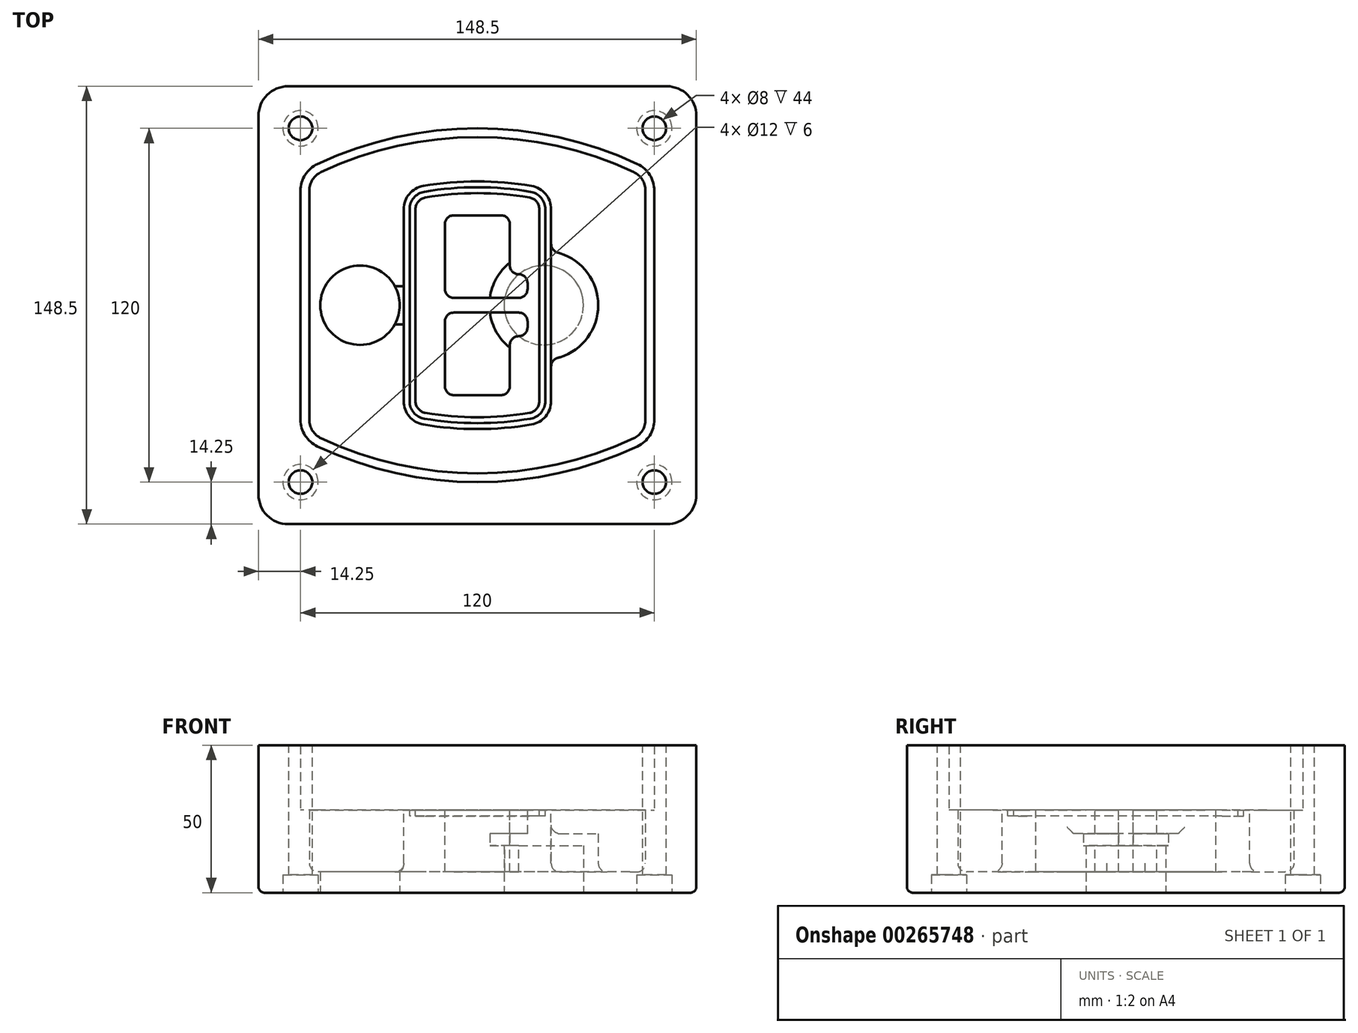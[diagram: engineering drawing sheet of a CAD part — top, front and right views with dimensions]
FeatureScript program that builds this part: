
annotation { "Feature Type Name" : "Feature", "Feature Type Description" : "" }
export const myFeature = defineFeature(function(context is Context, id is Id, definition is map)
    precondition{}
    {
        {
            var Q0;
            Q0=qCreatedBy(makeId("Top.planeOp"),FACE);
            var sketch = newSketch(context, id + "F0", { "sketchPlane" : qUnion([Q0])});
            skPoint(sketch, "E0.rect.middle", {"position": v(0, 0) * mm});
            skLineSegment(sketch, "E1.bottom", {"start": v(-64.25, -74.25) * mm, "end": v(64.25, -74.25) * mm});
            skLineSegment(sketch, "E1.top", {"start": v(-64.25, 74.25) * mm, "end": v(64.25, 74.25) * mm});
            skLineSegment(sketch, "E1.left", {"start": v(-74.25, -64.25) * mm, "end": v(-74.25, 64.25) * mm});
            skLineSegment(sketch, "E1.right", {"start": v(74.25, -64.25) * mm, "end": v(74.25, 64.25) * mm});
            skLineSegment(sketch, "E2", {"start": v(-74.25, 74.25) * mm, "end": v(74.25, -74.25) * mm, "construction": true});
            skLineSegment(sketch, "E3", {"start": v(74.25, 74.25) * mm, "end": v(-74.25, -74.25) * mm, "construction": true});
            skCircle(sketch, "E4", {"center": v(-60, 60) * mm, "radius": 4 * mm});
            skCircle(sketch, "E5", {"center": v(60, 60) * mm, "radius": 4 * mm});
            skCircle(sketch, "E6", {"center": v(60, -60) * mm, "radius": 4 * mm});
            skCircle(sketch, "E7", {"center": v(-60, -60) * mm, "radius": 4 * mm});
            skLineSegment(sketch, "E8", {"start": v(-60, 60) * mm, "end": v(60, 60) * mm, "construction": true});
            skLineSegment(sketch, "E9", {"start": v(60, 60) * mm, "end": v(60, -60) * mm, "construction": true});
            skLineSegment(sketch, "E10", {"start": v(60, -60) * mm, "end": v(-60, -60) * mm, "construction": true});
            skLineSegment(sketch, "E11", {"start": v(-60, -60) * mm, "end": v(-60, 60) * mm, "construction": true});
            skLineSegment(sketch, "E12", {"start": v(-60, 38.83) * mm, "end": v(-60, -38.83) * mm});
            skLineSegment(sketch, "E13", {"start": v(60, 38.83) * mm, "end": v(60, -38.83) * mm});
            skArc(sketch, "E14", {"start": v(54.26, 47.88) * mm, "mid": v(0, 60) * mm, "end": v(-54.26, 47.88) * mm});
            skArc(sketch, "E15", {"start": v(-54.26, -47.88) * mm, "mid": v(0, -60) * mm, "end": v(54.26, -47.88) * mm});
            skLineSegment(sketch, "E16", {"start": v(-60, 0) * mm, "end": v(60, 0) * mm, "construction": true});
            skPoint(sketch, "E17.visualSharp", {"position": v(-60, -45) * mm});
            skArc(sketch, "E17.filletArc", {"start": v(-60, -38.83) * mm, "mid": v(-58.44, -44.2) * mm, "end": v(-54.26, -47.88) * mm});
            skPoint(sketch, "E18.visualSharp", {"position": v(-60, 45) * mm});
            skArc(sketch, "E18.filletArc", {"start": v(-54.26, 47.88) * mm, "mid": v(-58.44, 44.2) * mm, "end": v(-60, 38.83) * mm});
            skPoint(sketch, "E19.visualSharp", {"position": v(60, 45) * mm});
            skArc(sketch, "E19.filletArc", {"start": v(60, 38.83) * mm, "mid": v(58.44, 44.2) * mm, "end": v(54.26, 47.88) * mm});
            skPoint(sketch, "E20.visualSharp", {"position": v(60, -45) * mm});
            skArc(sketch, "E20.filletArc", {"start": v(54.26, -47.88) * mm, "mid": v(58.44, -44.2) * mm, "end": v(60, -38.83) * mm});
            skPoint(sketch, "E21.visualSharp", {"position": v(-74.25, 74.25) * mm});
            skArc(sketch, "E21.filletArc", {"start": v(-64.25, 74.25) * mm, "mid": v(-71.32, 71.32) * mm, "end": v(-74.25, 64.25) * mm});
            skPoint(sketch, "E22.visualSharp", {"position": v(74.25, 74.25) * mm});
            skArc(sketch, "E22.filletArc", {"start": v(74.25, 64.25) * mm, "mid": v(71.32, 71.32) * mm, "end": v(64.25, 74.25) * mm});
            skPoint(sketch, "E23.visualSharp", {"position": v(74.25, -74.25) * mm});
            skArc(sketch, "E23.filletArc", {"start": v(64.25, -74.25) * mm, "mid": v(71.32, -71.32) * mm, "end": v(74.25, -64.25) * mm});
            skPoint(sketch, "E24.visualSharp", {"position": v(-74.25, -74.25) * mm});
            skArc(sketch, "E24.filletArc", {"start": v(-74.25, -64.25) * mm, "mid": v(-71.32, -71.32) * mm, "end": v(-64.25, -74.25) * mm});
            skArc(sketch, "E25.0", {"start": v(57, 38.83) * mm, "mid": v(55.9, 42.58) * mm, "end": v(52.98, 45.17) * mm});
            skLineSegment(sketch, "E25.1", {"start": v(57, 38.83) * mm, "end": v(57, -38.83) * mm});
            skArc(sketch, "E25.2", {"start": v(52.98, -45.17) * mm, "mid": v(55.9, -42.58) * mm, "end": v(57, -38.83) * mm});
            skArc(sketch, "E25.3", {"start": v(-52.98, -45.17) * mm, "mid": v(0, -57) * mm, "end": v(52.98, -45.17) * mm});
            skArc(sketch, "E25.4", {"start": v(-57, -38.83) * mm, "mid": v(-55.9, -42.58) * mm, "end": v(-52.98, -45.17) * mm});
            skArc(sketch, "E25.5", {"start": v(52.98, 45.17) * mm, "mid": v(0, 57) * mm, "end": v(-52.98, 45.17) * mm});
            skLineSegment(sketch, "E25.6", {"start": v(-57, 38.83) * mm, "end": v(-57, -38.83) * mm});
            skArc(sketch, "E25.7", {"start": v(-52.98, 45.17) * mm, "mid": v(-55.9, 42.58) * mm, "end": v(-57, 38.83) * mm});
            skArc(sketch, "E26.0", {"start": v(-55.96, 51.5) * mm, "mid": v(-61.82, 46.33) * mm, "end": v(-64, 38.83) * mm});
            skArc(sketch, "E26.1", {"start": v(55.96, 51.5) * mm, "mid": v(0, 64) * mm, "end": v(-55.96, 51.5) * mm});
            skArc(sketch, "E26.2", {"start": v(64, 38.83) * mm, "mid": v(61.82, 46.33) * mm, "end": v(55.96, 51.5) * mm});
            skLineSegment(sketch, "E26.3", {"start": v(64, 38.83) * mm, "end": v(64, -38.83) * mm});
            skArc(sketch, "E26.4", {"start": v(55.96, -51.5) * mm, "mid": v(61.82, -46.33) * mm, "end": v(64, -38.83) * mm});
            skLineSegment(sketch, "E26.5", {"start": v(-64, 38.83) * mm, "end": v(-64, -38.83) * mm});
            skArc(sketch, "E26.6", {"start": v(-55.96, -51.5) * mm, "mid": v(0, -64) * mm, "end": v(55.96, -51.5) * mm});
            skArc(sketch, "E26.7", {"start": v(-64, -38.83) * mm, "mid": v(-61.82, -46.33) * mm, "end": v(-55.96, -51.5) * mm});
            skSolve(sketch);
        }
        {
            var Q0;
            Q0=makeQuery(id+"F0.imprint","IMPRINT",FACE,{"disambiguationData":[TD([[makeQuery(id+"F0.imprint","IMPRINT",EDGE,{"derivedFrom":sQuery(id+"F0.wireOp",EDGE,"E1.bottom")}),1.0]])]});
            var Q1;
            Q1=makeQuery(id+"F0.imprint","IMPRINT",FACE,{"disambiguationData":[TD([[makeQuery(id+"F0.imprint","IMPRINT",EDGE,{"derivedFrom":sQuery(id+"F0.wireOp",EDGE,"E12")}),1.0]])]});
            var Q2;
            Q2=makeQuery(id+"F0.imprint","IMPRINT",FACE,{"disambiguationData":[TD([[makeQuery(id+"F0.imprint","IMPRINT",EDGE,{"derivedFrom":sQuery(id+"F0.wireOp",EDGE,"E25.0")}),1.0]])]});
            var Q3;
            Q3=makeQuery(id+"F0.imprint","IMPRINT",FACE,{"disambiguationData":[TD([[makeQuery(id+"F0.imprint","IMPRINT",EDGE,{"derivedFrom":sQuery(id+"F0.wireOp",EDGE,"E12")}),-1.0]])]});
            extrude(context, id + "F1", {"entities" : qUnion([Q0, Q1, Q2, Q3]), "oppositeDirection" : true, "depth" : 25 * mm});
        }
        {
            var Q0;
            Q0=makeQuery(id+"F0.imprint","IMPRINT",FACE,{"disambiguationData":[TD([[makeQuery(id+"F0.imprint","IMPRINT",EDGE,{"derivedFrom":sQuery(id+"F0.wireOp",EDGE,"E12")}),1.0]])]});
            extrude(context, id + "F2", {"entities" : qUnion([Q0]), "operationType" : NewBodyOperationType.ADD, "depth" : 3 * mm});
        }
        {
            var Q0;
            Q0=makeQuery(id+"F0.imprint","IMPRINT",FACE,{"disambiguationData":[TD([[makeQuery(id+"F0.imprint","IMPRINT",EDGE,{"derivedFrom":sQuery(id+"F0.wireOp",EDGE,"E25.0")}),1.0]])]});
            extrude(context, id + "F3", {"entities" : qUnion([Q0]), "operationType" : NewBodyOperationType.REMOVE, "oppositeDirection" : true, "depth" : 18 * mm});
        }
        {
            var Q0;
            Q0=makeQuery(id+"F2.opExtrude","CAP_FACE",FACE,{"disambiguationData":[OSD([sQuery(id+"F0.wireOp",EDGE,"E12"),sQuery(id+"F0.wireOp",EDGE,"E13"),sQuery(id+"F0.wireOp",EDGE,"E14"),sQuery(id+"F0.wireOp",EDGE,"E15"),sQuery(id+"F0.wireOp",EDGE,"E17.filletArc"),sQuery(id+"F0.wireOp",EDGE,"E18.filletArc"),sQuery(id+"F0.wireOp",EDGE,"E19.filletArc"),sQuery(id+"F0.wireOp",EDGE,"E20.filletArc"),sQuery(id+"F0.wireOp",EDGE,"E25.0"),sQuery(id+"F0.wireOp",EDGE,"E25.1"),sQuery(id+"F0.wireOp",EDGE,"E25.2"),sQuery(id+"F0.wireOp",EDGE,"E25.3"),sQuery(id+"F0.wireOp",EDGE,"E25.4"),sQuery(id+"F0.wireOp",EDGE,"E25.5"),sQuery(id+"F0.wireOp",EDGE,"E25.6"),sQuery(id+"F0.wireOp",EDGE,"E25.7")])],"isStart":false});
            var sketch = newSketch(context, id + "F4", { "sketchPlane" : qUnion([Q0])});
            skArc(sketch, "E27.0", {"start": v(-18.34, -40.45) * mm, "mid": v(0, -42) * mm, "end": v(18.34, -40.45) * mm});
            skArc(sketch, "E28.0", {"start": v(18.34, 40.45) * mm, "mid": v(0, 42) * mm, "end": v(-18.34, 40.45) * mm});
            skLineSegment(sketch, "E29", {"start": v(-25, 32.57) * mm, "end": v(-25, -32.57) * mm});
            skLineSegment(sketch, "E30", {"start": v(25, 32.57) * mm, "end": v(25, -32.57) * mm});
            skLineSegment(sketch, "E31", {"start": v(-25, 39.1) * mm, "end": v(25, 39.1) * mm, "construction": true});
            skLineSegment(sketch, "E32", {"start": v(-25, -39.1) * mm, "end": v(25, -39.1) * mm, "construction": true});
            skPoint(sketch, "E33.visualSharp", {"position": v(-25, 39.1) * mm});
            skArc(sketch, "E33.filletArc", {"start": v(-18.34, 40.45) * mm, "mid": v(-23.11, 37.73) * mm, "end": v(-25, 32.57) * mm});
            skPoint(sketch, "E34.visualSharp", {"position": v(25, 39.1) * mm});
            skArc(sketch, "E34.filletArc", {"start": v(25, 32.57) * mm, "mid": v(23.11, 37.73) * mm, "end": v(18.34, 40.45) * mm});
            skPoint(sketch, "E35.visualSharp", {"position": v(25, -39.1) * mm});
            skArc(sketch, "E35.filletArc", {"start": v(18.34, -40.45) * mm, "mid": v(23.11, -37.73) * mm, "end": v(25, -32.57) * mm});
            skPoint(sketch, "E36.visualSharp", {"position": v(-25, -39.1) * mm});
            skArc(sketch, "E36.filletArc", {"start": v(-25, -32.57) * mm, "mid": v(-23.11, -37.73) * mm, "end": v(-18.34, -40.45) * mm});
            skArc(sketch, "E37.0", {"start": v(52.98, 45.17) * mm, "mid": v(0, 57) * mm, "end": v(-52.98, 45.17) * mm});
            skArc(sketch, "E37.1", {"start": v(-52.98, 45.17) * mm, "mid": v(-55.9, 42.58) * mm, "end": v(-57, 38.83) * mm});
            skLineSegment(sketch, "E37.2", {"start": v(-57, 38.83) * mm, "end": v(-57, -38.83) * mm});
            skArc(sketch, "E37.3", {"start": v(-57, -38.83) * mm, "mid": v(-55.9, -42.58) * mm, "end": v(-52.98, -45.17) * mm});
            skArc(sketch, "E37.4", {"start": v(-52.98, -45.17) * mm, "mid": v(0, -57) * mm, "end": v(52.98, -45.17) * mm});
            skArc(sketch, "E37.5", {"start": v(52.98, -45.17) * mm, "mid": v(55.9, -42.58) * mm, "end": v(57, -38.83) * mm});
            skLineSegment(sketch, "E37.6", {"start": v(57, 38.83) * mm, "end": v(57, -38.83) * mm});
            skArc(sketch, "E37.7", {"start": v(57, 38.83) * mm, "mid": v(55.9, 42.58) * mm, "end": v(52.98, 45.17) * mm});
            skLineSegment(sketch, "E38.0", {"start": v(23, 32.57) * mm, "end": v(23, -32.57) * mm});
            skArc(sketch, "E38.1", {"start": v(18, -38.48) * mm, "mid": v(21.58, -36.44) * mm, "end": v(23, -32.57) * mm});
            skArc(sketch, "E38.2", {"start": v(-18, -38.48) * mm, "mid": v(0, -40) * mm, "end": v(18, -38.48) * mm});
            skArc(sketch, "E38.3", {"start": v(-23, -32.57) * mm, "mid": v(-21.58, -36.44) * mm, "end": v(-18, -38.48) * mm});
            skLineSegment(sketch, "E38.4", {"start": v(-23, 32.57) * mm, "end": v(-23, -32.57) * mm});
            skArc(sketch, "E38.5", {"start": v(23, 32.57) * mm, "mid": v(21.58, 36.44) * mm, "end": v(18, 38.48) * mm});
            skArc(sketch, "E38.6", {"start": v(-18, 38.48) * mm, "mid": v(-21.58, 36.44) * mm, "end": v(-23, 32.57) * mm});
            skArc(sketch, "E38.7", {"start": v(18, 38.48) * mm, "mid": v(0, 40) * mm, "end": v(-18, 38.48) * mm});
            skArc(sketch, "E39.0", {"start": v(21, 32.57) * mm, "mid": v(20.06, 35.15) * mm, "end": v(17.67, 36.5) * mm});
            skLineSegment(sketch, "E39.1", {"start": v(21, 32.57) * mm, "end": v(21, -32.57) * mm});
            skArc(sketch, "E39.2", {"start": v(17.67, -36.5) * mm, "mid": v(20.06, -35.15) * mm, "end": v(21, -32.57) * mm});
            skArc(sketch, "E39.3", {"start": v(-17.67, -36.5) * mm, "mid": v(0, -38) * mm, "end": v(17.67, -36.5) * mm});
            skArc(sketch, "E39.4", {"start": v(-21, -32.57) * mm, "mid": v(-20.06, -35.15) * mm, "end": v(-17.67, -36.5) * mm});
            skArc(sketch, "E39.5", {"start": v(17.67, 36.5) * mm, "mid": v(0, 38) * mm, "end": v(-17.67, 36.5) * mm});
            skLineSegment(sketch, "E39.6", {"start": v(-21, 32.57) * mm, "end": v(-21, -32.57) * mm});
            skArc(sketch, "E39.7", {"start": v(-17.67, 36.5) * mm, "mid": v(-20.06, 35.15) * mm, "end": v(-21, 32.57) * mm});
            skLineSegment(sketch, "E40", {"start": v(-25, 0) * mm, "end": v(25, 0) * mm, "construction": true});
            skLineSegment(sketch, "E41", {"start": v(-11, 5.5) * mm, "end": v(-11, 27.5) * mm});
            skLineSegment(sketch, "E42", {"start": v(-8, 30.5) * mm, "end": v(8, 30.5) * mm});
            skLineSegment(sketch, "E43", {"start": v(11, 27.5) * mm, "end": v(11, 13.5) * mm});
            skLineSegment(sketch, "E44", {"start": v(14, 10.5) * mm, "end": v(14, 10.5) * mm});
            skLineSegment(sketch, "E45", {"start": v(17, 7.5) * mm, "end": v(17, 5.5) * mm});
            skLineSegment(sketch, "E46", {"start": v(14, 2.5) * mm, "end": v(-8, 2.5) * mm});
            skPoint(sketch, "E47.visualSharp", {"position": v(-11, 30.5) * mm});
            skArc(sketch, "E47.filletArc", {"start": v(-8, 30.5) * mm, "mid": v(-10.12, 29.62) * mm, "end": v(-11, 27.5) * mm});
            skPoint(sketch, "E48.visualSharp", {"position": v(11, 30.5) * mm});
            skArc(sketch, "E48.filletArc", {"start": v(11, 27.5) * mm, "mid": v(10.12, 29.62) * mm, "end": v(8, 30.5) * mm});
            skPoint(sketch, "E49.visualSharp", {"position": v(11, 10.5) * mm});
            skArc(sketch, "E49.filletArc", {"start": v(11, 13.5) * mm, "mid": v(11.88, 11.38) * mm, "end": v(14, 10.5) * mm});
            skPoint(sketch, "E50.visualSharp", {"position": v(17, 10.5) * mm});
            skArc(sketch, "E50.filletArc", {"start": v(17, 7.5) * mm, "mid": v(16.12, 9.62) * mm, "end": v(14, 10.5) * mm});
            skPoint(sketch, "E51.visualSharp", {"position": v(17, 2.5) * mm});
            skArc(sketch, "E51.filletArc", {"start": v(14, 2.5) * mm, "mid": v(16.12, 3.38) * mm, "end": v(17, 5.5) * mm});
            skPoint(sketch, "E52.visualSharp", {"position": v(-11, 2.5) * mm});
            skArc(sketch, "E52.filletArc", {"start": v(-11, 5.5) * mm, "mid": v(-10.12, 3.38) * mm, "end": v(-8, 2.5) * mm});
            skLineSegment(sketch, "E53.0.MirrorCS", {"start": v(14, -2.5) * mm, "end": v(-8, -2.5) * mm});
            skArc(sketch, "E54.0.MirrorCS", {"start": v(-11, -5.5) * mm, "mid": v(-10.12, -3.38) * mm, "end": v(-8, -2.5) * mm});
            skLineSegment(sketch, "E55.0.MirrorCS", {"start": v(-11, -5.5) * mm, "end": v(-11, -27.5) * mm});
            skArc(sketch, "E56.0.MirrorCS", {"start": v(-8, -30.5) * mm, "mid": v(-10.12, -29.62) * mm, "end": v(-11, -27.5) * mm});
            skLineSegment(sketch, "E57.0.MirrorCS", {"start": v(-8, -30.5) * mm, "end": v(8, -30.5) * mm});
            skArc(sketch, "E58.0.MirrorCS", {"start": v(11, -27.5) * mm, "mid": v(10.12, -29.62) * mm, "end": v(8, -30.5) * mm});
            skLineSegment(sketch, "E59.0.MirrorCS", {"start": v(11, -27.5) * mm, "end": v(11, -13.5) * mm});
            skArc(sketch, "E60.0.MirrorCS", {"start": v(11, -13.5) * mm, "mid": v(11.88, -11.38) * mm, "end": v(14, -10.5) * mm});
            skArc(sketch, "E61.0.MirrorCS", {"start": v(17, -7.5) * mm, "mid": v(16.12, -9.62) * mm, "end": v(14, -10.5) * mm});
            skLineSegment(sketch, "E62.0.MirrorCS", {"start": v(17, -7.5) * mm, "end": v(17, -5.5) * mm});
            skArc(sketch, "E63.0.MirrorCS", {"start": v(14, -2.5) * mm, "mid": v(16.12, -3.38) * mm, "end": v(17, -5.5) * mm});
            skSolve(sketch);
        }
        {
            var Q0;
            Q0=makeQuery(id+"F4.imprint","IMPRINT",FACE,{"disambiguationData":[TD([[makeQuery(id+"F4.imprint","IMPRINT",EDGE,{"derivedFrom":sQuery(id+"F4.wireOp",EDGE,"E27.0")}),1.0]])]});
            var Q1;
            Q1=makeQuery(id+"F4.imprint","IMPRINT",FACE,{"disambiguationData":[TD([[makeQuery(id+"F4.imprint","IMPRINT",EDGE,{"derivedFrom":sQuery(id+"F4.wireOp",EDGE,"E38.0")}),-1.0]])]});
            var Q2;
            Q2=makeQuery(id+"F4.imprint","IMPRINT",FACE,{"disambiguationData":[TD([[makeQuery(id+"F4.imprint","IMPRINT",EDGE,{"derivedFrom":sQuery(id+"F4.wireOp",EDGE,"E39.0")}),1.0]])]});
            extrude(context, id + "F5", {"entities" : qUnion([Q0, Q1, Q2]), "operationType" : NewBodyOperationType.ADD, "endBound" : BoundingType.UP_TO_NEXT, "oppositeDirection" : true, "depth" : 25 * mm});
        }
        {
            var Q0;
            Q0=makeQuery(id+"F4.imprint","IMPRINT",FACE,{"disambiguationData":[TD([[makeQuery(id+"F4.imprint","IMPRINT",EDGE,{"derivedFrom":sQuery(id+"F4.wireOp",EDGE,"E38.0")}),-1.0]])]});
            extrude(context, id + "F6", {"entities" : qUnion([Q0]), "operationType" : NewBodyOperationType.REMOVE, "oppositeDirection" : true, "depth" : 2 * mm});
        }
        {
            var Q0;
            Q0=makeQuery(id+"F1.opExtrude","CAP_FACE",FACE,{"disambiguationData":[OSD([sQuery(id+"F0.wireOp",EDGE,"E1.bottom"),sQuery(id+"F0.wireOp",EDGE,"E1.top"),sQuery(id+"F0.wireOp",EDGE,"E1.left"),sQuery(id+"F0.wireOp",EDGE,"E1.right"),sQuery(id+"F0.wireOp",EDGE,"E4"),sQuery(id+"F0.wireOp",EDGE,"E5"),sQuery(id+"F0.wireOp",EDGE,"E6"),sQuery(id+"F0.wireOp",EDGE,"E7"),sQuery(id+"F0.wireOp",EDGE,"E21.filletArc"),sQuery(id+"F0.wireOp",EDGE,"E22.filletArc"),sQuery(id+"F0.wireOp",EDGE,"E23.filletArc"),sQuery(id+"F0.wireOp",EDGE,"E24.filletArc")])],"isStart":false});
            var sketch = newSketch(context, id + "F7", { "sketchPlane" : qUnion([Q0])});
            skCircle(sketch, "E64", {"center": v(22.5, 0) * mm, "radius": 13.47 * mm});
            skCircle(sketch, "E65", {"center": v(-39.81, 0) * mm, "radius": 13.47 * mm});
            skLineSegment(sketch, "E66", {"start": v(74.25, 0) * mm, "end": v(-74.25, 0) * mm});
            skCircle(sketch, "E67", {"center": v(22.5, 0) * mm, "radius": 18.47 * mm});
            skCircle(sketch, "E68", {"center": v(60, -60) * mm, "radius": 6 * mm});
            skCircle(sketch, "E69", {"center": v(-60, -60) * mm, "radius": 6 * mm});
            skCircle(sketch, "E70", {"center": v(-60, 60) * mm, "radius": 6 * mm});
            skCircle(sketch, "E71", {"center": v(60, 60) * mm, "radius": 6 * mm});
            skSolve(sketch);
        }
        {
            var Q0;
            {var subQ1=sQuery(id+"F7.wireOp",EDGE,"E66");var subQ4=sQuery(id+"F7.wireOp",EDGE,"E64");var subQ6=makeQuery(id+"F7.imprint","INTERSECT",VERTEX,{"disambiguationData":[OD(0.0)],"derivedFrom":[subQ4,subQ1]});Q0=makeQuery(id+"F7.imprint","IMPRINT",FACE,{"disambiguationData":[TD([[makeQuery(id+"F7.imprint","IMPRINT",EDGE,{"disambiguationData":[TD([[subQ6,-1.0]])],"derivedFrom":subQ4}),-1.0]])]});}
            var Q1;
            {var subQ0=sQuery(id+"F7.wireOp",EDGE,"E66");var subQ1=sQuery(id+"F7.wireOp",EDGE,"E64");var subQ3=makeQuery(id+"F7.imprint","INTERSECT",VERTEX,{"disambiguationData":[OD(0.0)],"derivedFrom":[subQ1,subQ0]});Q1=makeQuery(id+"F7.imprint","IMPRINT",FACE,{"disambiguationData":[TD([[makeQuery(id+"F7.imprint","IMPRINT",EDGE,{"disambiguationData":[TD([[subQ3,-1.0]])],"derivedFrom":subQ1}),1.0]])]});}
            var Q2;
            {var subQ0=sQuery(id+"F7.wireOp",EDGE,"E66");var subQ1=sQuery(id+"F7.wireOp",EDGE,"E64");var subQ3=makeQuery(id+"F7.imprint","INTERSECT",VERTEX,{"disambiguationData":[OD(0.0)],"derivedFrom":[subQ1,subQ0]});Q2=makeQuery(id+"F7.imprint","IMPRINT",FACE,{"disambiguationData":[TD([[makeQuery(id+"F7.imprint","IMPRINT",EDGE,{"disambiguationData":[TD([[subQ3,1.0]])],"derivedFrom":subQ1}),1.0]])]});}
            var Q3;
            {var subQ1=sQuery(id+"F7.wireOp",EDGE,"E66");var subQ4=sQuery(id+"F7.wireOp",EDGE,"E64");var subQ6=makeQuery(id+"F7.imprint","INTERSECT",VERTEX,{"disambiguationData":[OD(0.0)],"derivedFrom":[subQ4,subQ1]});Q3=makeQuery(id+"F7.imprint","IMPRINT",FACE,{"disambiguationData":[TD([[makeQuery(id+"F7.imprint","IMPRINT",EDGE,{"disambiguationData":[TD([[subQ6,1.0]])],"derivedFrom":subQ4}),-1.0]])]});}
            extrude(context, id + "F8", {"entities" : qUnion([Q0, Q1, Q2, Q3]), "operationType" : NewBodyOperationType.ADD, "oppositeDirection" : true, "depth" : 20 * mm});
        }
        {
            var Q0;
            {var subQ0=sQuery(id+"F7.wireOp",EDGE,"E66");var subQ1=sQuery(id+"F7.wireOp",EDGE,"E64");var subQ3=makeQuery(id+"F7.imprint","INTERSECT",VERTEX,{"disambiguationData":[OD(0.0)],"derivedFrom":[subQ1,subQ0]});Q0=makeQuery(id+"F7.imprint","IMPRINT",FACE,{"disambiguationData":[TD([[makeQuery(id+"F7.imprint","IMPRINT",EDGE,{"disambiguationData":[TD([[subQ3,-1.0]])],"derivedFrom":subQ1}),1.0]])]});}
            var Q1;
            {var subQ0=sQuery(id+"F7.wireOp",EDGE,"E66");var subQ1=sQuery(id+"F7.wireOp",EDGE,"E64");var subQ3=makeQuery(id+"F7.imprint","INTERSECT",VERTEX,{"disambiguationData":[OD(0.0)],"derivedFrom":[subQ1,subQ0]});Q1=makeQuery(id+"F7.imprint","IMPRINT",FACE,{"disambiguationData":[TD([[makeQuery(id+"F7.imprint","IMPRINT",EDGE,{"disambiguationData":[TD([[subQ3,1.0]])],"derivedFrom":subQ1}),1.0]])]});}
            extrude(context, id + "F9", {"entities" : qUnion([Q0, Q1]), "operationType" : NewBodyOperationType.REMOVE, "oppositeDirection" : true, "depth" : 16 * mm});
        }
        {
            var Q0;
            {var subQ0=sQuery(id+"F7.wireOp",EDGE,"E66");var subQ1=sQuery(id+"F7.wireOp",EDGE,"E65");var subQ3=makeQuery(id+"F7.imprint","INTERSECT",VERTEX,{"disambiguationData":[OD(0.0)],"derivedFrom":[subQ1,subQ0]});Q0=makeQuery(id+"F7.imprint","IMPRINT",FACE,{"disambiguationData":[TD([[makeQuery(id+"F7.imprint","IMPRINT",EDGE,{"disambiguationData":[TD([[subQ3,-1.0]])],"derivedFrom":subQ1}),1.0]])]});}
            var Q1;
            {var subQ0=sQuery(id+"F7.wireOp",EDGE,"E66");var subQ1=sQuery(id+"F7.wireOp",EDGE,"E65");var subQ3=makeQuery(id+"F7.imprint","INTERSECT",VERTEX,{"disambiguationData":[OD(0.0)],"derivedFrom":[subQ1,subQ0]});Q1=makeQuery(id+"F7.imprint","IMPRINT",FACE,{"disambiguationData":[TD([[makeQuery(id+"F7.imprint","IMPRINT",EDGE,{"disambiguationData":[TD([[subQ3,1.0]])],"derivedFrom":subQ1}),1.0]])]});}
            extrude(context, id + "F10", {"entities" : qUnion([Q0, Q1]), "operationType" : NewBodyOperationType.REMOVE, "oppositeDirection" : true, "depth" : 25 * mm});
        }
        {
            var Q0;
            Q0=makeQuery(id+"F7.imprint","IMPRINT",FACE,{"disambiguationData":[TD([[makeQuery(id+"F7.imprint","IMPRINT",EDGE,{"derivedFrom":sQuery(id+"F7.wireOp",EDGE,"E68")}),1.0]])]});
            var Q1;
            Q1=makeQuery(id+"F7.imprint","IMPRINT",FACE,{"disambiguationData":[TD([[makeQuery(id+"F7.imprint","IMPRINT",EDGE,{"derivedFrom":makeQuery(id+"F1.opExtrude","CAP_EDGE",EDGE,{"disambiguationData":[OSD([sQuery(id+"F0.wireOp",EDGE,"E5")])],"isStart":false})}),-1.0]])]});
            var Q2;
            Q2=makeQuery(id+"F7.imprint","IMPRINT",FACE,{"disambiguationData":[TD([[makeQuery(id+"F7.imprint","IMPRINT",EDGE,{"derivedFrom":sQuery(id+"F7.wireOp",EDGE,"E69")}),1.0]])]});
            var Q3;
            Q3=makeQuery(id+"F7.imprint","IMPRINT",FACE,{"disambiguationData":[TD([[makeQuery(id+"F7.imprint","IMPRINT",EDGE,{"derivedFrom":makeQuery(id+"F1.opExtrude","CAP_EDGE",EDGE,{"disambiguationData":[OSD([sQuery(id+"F0.wireOp",EDGE,"E4")])],"isStart":false})}),-1.0]])]});
            var Q4;
            Q4=makeQuery(id+"F7.imprint","IMPRINT",FACE,{"disambiguationData":[TD([[makeQuery(id+"F7.imprint","IMPRINT",EDGE,{"derivedFrom":sQuery(id+"F7.wireOp",EDGE,"E70")}),1.0]])]});
            var Q5;
            Q5=makeQuery(id+"F7.imprint","IMPRINT",FACE,{"disambiguationData":[TD([[makeQuery(id+"F7.imprint","IMPRINT",EDGE,{"derivedFrom":makeQuery(id+"F1.opExtrude","CAP_EDGE",EDGE,{"disambiguationData":[OSD([sQuery(id+"F0.wireOp",EDGE,"E7")])],"isStart":false})}),-1.0]])]});
            var Q6;
            Q6=makeQuery(id+"F7.imprint","IMPRINT",FACE,{"disambiguationData":[TD([[makeQuery(id+"F7.imprint","IMPRINT",EDGE,{"derivedFrom":sQuery(id+"F7.wireOp",EDGE,"E71")}),1.0]])]});
            var Q7;
            Q7=makeQuery(id+"F7.imprint","IMPRINT",FACE,{"disambiguationData":[TD([[makeQuery(id+"F7.imprint","IMPRINT",EDGE,{"derivedFrom":makeQuery(id+"F1.opExtrude","CAP_EDGE",EDGE,{"disambiguationData":[OSD([sQuery(id+"F0.wireOp",EDGE,"E6")])],"isStart":false})}),-1.0]])]});
            extrude(context, id + "F11", {"entities" : qUnion([Q0, Q1, Q2, Q3, Q4, Q5, Q6, Q7]), "operationType" : NewBodyOperationType.REMOVE, "oppositeDirection" : true, "depth" : 6 * mm});
        }
        {
            var Q0;
            Q0=makeQuery(id+"F9.boolean.opBoolean","COPY",FACE,{"derivedFrom":makeQuery(id+"F9.opExtrude","CAP_FACE",FACE,{"disambiguationData":[OSD([sQuery(id+"F7.wireOp",EDGE,"E64")])],"isStart":false})});
            var sketch = newSketch(context, id + "F12", { "sketchPlane" : qUnion([Q0])});
            skArc(sketch, "E72.0", {"start": v(11, 14.45) * mm, "mid": v(6.45, 9.13) * mm, "end": v(4.2, 2.5) * mm});
            skArc(sketch, "E72.1", {"start": v(4.2, -2.5) * mm, "mid": v(6.45, -9.13) * mm, "end": v(11, -14.45) * mm});
            skLineSegment(sketch, "E73", {"start": v(4.2, -2.5) * mm, "end": v(14, -2.5) * mm});
            skLineSegment(sketch, "E74.0", {"start": v(14, 2.5) * mm, "end": v(4.2, 2.5) * mm});
            skArc(sketch, "E74.1", {"start": v(14, 2.5) * mm, "mid": v(16.12, 3.38) * mm, "end": v(17, 5.5) * mm});
            skLineSegment(sketch, "E74.2", {"start": v(17, 7.5) * mm, "end": v(17, 5.5) * mm});
            skArc(sketch, "E74.3", {"start": v(17, 7.5) * mm, "mid": v(16.12, 9.62) * mm, "end": v(14, 10.5) * mm});
            skArc(sketch, "E74.4", {"start": v(11, 13.5) * mm, "mid": v(11.88, 11.38) * mm, "end": v(14, 10.5) * mm});
            skLineSegment(sketch, "E74.5", {"start": v(11, 14.45) * mm, "end": v(11, 13.5) * mm});
            skLineSegment(sketch, "E74.7", {"start": v(14, -2.5) * mm, "end": v(4.2, -2.5) * mm});
            skArc(sketch, "E74.8", {"start": v(14, -2.5) * mm, "mid": v(16.12, -3.38) * mm, "end": v(17, -5.5) * mm});
            skLineSegment(sketch, "E74.9", {"start": v(17, -7.5) * mm, "end": v(17, -5.5) * mm});
            skArc(sketch, "E74.10", {"start": v(17, -7.5) * mm, "mid": v(16.12, -9.62) * mm, "end": v(14, -10.5) * mm});
            skArc(sketch, "E74.11", {"start": v(11, -13.5) * mm, "mid": v(11.88, -11.38) * mm, "end": v(14, -10.5) * mm});
            skLineSegment(sketch, "E74.12", {"start": v(11, -14.45) * mm, "end": v(11, -13.5) * mm});
            skPoint(sketch, "E75.orphan", {"position": v(11, -27.5) * mm});
            skPoint(sketch, "E76.orphan", {"position": v(-8, -2.5) * mm});
            skPoint(sketch, "E77.orphan", {"position": v(-8, 2.5) * mm});
            skPoint(sketch, "E78.orphan", {"position": v(11, 27.5) * mm});
            skSolve(sketch);
        }
        {
            var Q0;
            {var subQ7=sQuery(id+"F12.wireOp",EDGE,"E72.0");var subQ14=sQuery(id+"F12.wireOp",EDGE,"E72.1");var subQ16=sQuery(id+"F12.wireOp",EDGE,"E74.1");var subQ18=sQuery(id+"F12.wireOp",EDGE,"E74.8");Q0=qUnion([makeQuery(id+"F12.imprint","IMPRINT",FACE,{"disambiguationData":[TD([[makeQuery(id+"F12.imprint","IMPRINT",EDGE,{"derivedFrom":subQ7}),1.0]])]}),makeQuery(id+"F12.imprint","IMPRINT",FACE,{"disambiguationData":[TD([[makeQuery(id+"F12.imprint","IMPRINT",EDGE,{"derivedFrom":subQ14}),1.0]])]}),makeQuery(id+"F12.imprint","IMPRINT",FACE,{"disambiguationData":[TD([[makeQuery(id+"F12.imprint","IMPRINT",EDGE,{"derivedFrom":subQ16}),1.0]])]}),makeQuery(id+"F12.imprint","IMPRINT",FACE,{"disambiguationData":[TD([[makeQuery(id+"F12.imprint","IMPRINT",EDGE,{"derivedFrom":subQ18}),-1.0]])]})]);}
            var Q1;
            Q1=makeQuery(id+"F5.boolean.opBoolean","SPLIT",FACE,{"disambiguationData":[TD([makeQuery(id+"F5.opExtrude","SWEPT_FACE",FACE,{"disambiguationData":[OSD([sQuery(id+"F4.wireOp",EDGE,"E41")])]})])],"derivedFrom":makeQuery(id+"F3.boolean.opBoolean","COPY",FACE,{"derivedFrom":makeQuery(id+"F3.opExtrude","CAP_FACE",FACE,{"disambiguationData":[OSD([sQuery(id+"F0.wireOp",EDGE,"E25.0"),sQuery(id+"F0.wireOp",EDGE,"E25.1"),sQuery(id+"F0.wireOp",EDGE,"E25.2"),sQuery(id+"F0.wireOp",EDGE,"E25.3"),sQuery(id+"F0.wireOp",EDGE,"E25.4"),sQuery(id+"F0.wireOp",EDGE,"E25.5"),sQuery(id+"F0.wireOp",EDGE,"E25.6"),sQuery(id+"F0.wireOp",EDGE,"E25.7")])],"isStart":false})})});
            extrude(context, id + "F13", {"entities" : qUnion([Q0]), "operationType" : NewBodyOperationType.REMOVE, "endBound" : BoundingType.UP_TO_SURFACE, "endBoundEntityFace" : qUnion([Q1]), "depth" : 25 * mm});
        }
        {
            var Q0;
            Q0=makeQuery(id+"F3.boolean.opBoolean","COPY",EDGE,{"derivedFrom":makeQuery(id+"F3.opExtrude","CAP_EDGE",EDGE,{"disambiguationData":[OSD([sQuery(id+"F0.wireOp",EDGE,"E25.6")])],"isStart":false})});
            var Q1;
            Q1=makeQuery(id+"F8.boolean.opBoolean","INTERSECT",EDGE,{"derivedFrom":[makeQuery(id+"F5.opExtrude","SWEPT_FACE",FACE,{"disambiguationData":[OSD([sQuery(id+"F4.wireOp",EDGE,"E30")])]}),makeQuery(id+"F8.opExtrude","CAP_FACE",FACE,{"disambiguationData":[OSD([sQuery(id+"F7.wireOp",EDGE,"E67")])],"isStart":false})]});
            var Q2;
            Q2=makeQuery(id+"F8.boolean.opBoolean","INTERSECT",EDGE,{"disambiguationData":[OD(1.0)],"derivedFrom":[makeQuery(id+"F5.opExtrude","SWEPT_FACE",FACE,{"disambiguationData":[OSD([sQuery(id+"F4.wireOp",EDGE,"E30")])]}),makeQuery(id+"F8.opExtrude","SWEPT_FACE",FACE,{"disambiguationData":[OSD([sQuery(id+"F7.wireOp",EDGE,"E67")])]})]});
            var Q3;
            {var subQ0=sQuery(id+"F4.wireOp",EDGE,"E30");Q3=makeQuery(id+"F8.boolean.opBoolean","SPLIT",EDGE,{"disambiguationData":[TD([makeQuery(id+"F5.opExtrude","SWEPT_FACE",FACE,{"disambiguationData":[OSD([sQuery(id+"F4.wireOp",EDGE,"E35.filletArc")])]})])],"derivedFrom":makeQuery(id+"F5.opExtrude","CAP_EDGE",EDGE,{"disambiguationData":[OSD([subQ0])],"isStart":false})});}
            var Q4;
            {var subQ0=sQuery(id+"F0.wireOp",EDGE,"E25.7");var subQ1=sQuery(id+"F0.wireOp",EDGE,"E25.1");var subQ2=sQuery(id+"F0.wireOp",EDGE,"E25.6");var subQ3=sQuery(id+"F0.wireOp",EDGE,"E25.5");var subQ4=sQuery(id+"F0.wireOp",EDGE,"E25.4");var subQ5=sQuery(id+"F0.wireOp",EDGE,"E25.0");var subQ6=sQuery(id+"F0.wireOp",EDGE,"E25.2");var subQ7=sQuery(id+"F0.wireOp",EDGE,"E25.3");Q4=makeQuery(id+"F8.boolean.opBoolean","INTERSECT",EDGE,{"derivedFrom":[makeQuery(id+"F5.boolean.opBoolean","SPLIT",FACE,{"disambiguationData":[TD([makeQuery(id+"F2.opExtrude","SWEPT_FACE",FACE,{"disambiguationData":[OSD([subQ5])]})])],"derivedFrom":makeQuery(id+"F3.boolean.opBoolean","COPY",FACE,{"derivedFrom":makeQuery(id+"F3.opExtrude","CAP_FACE",FACE,{"disambiguationData":[OSD([subQ5,subQ1,subQ6,subQ7,subQ4,subQ3,subQ2,subQ0])],"isStart":false})})}),makeQuery(id+"F8.opExtrude","SWEPT_FACE",FACE,{"disambiguationData":[OSD([sQuery(id+"F7.wireOp",EDGE,"E67")])]})]});}
            var Q5;
            Q5=makeQuery(id+"F8.boolean.opBoolean","INTERSECT",EDGE,{"disambiguationData":[OD(0.0)],"derivedFrom":[makeQuery(id+"F5.opExtrude","SWEPT_FACE",FACE,{"disambiguationData":[OSD([sQuery(id+"F4.wireOp",EDGE,"E30")])]}),makeQuery(id+"F8.opExtrude","SWEPT_FACE",FACE,{"disambiguationData":[OSD([sQuery(id+"F7.wireOp",EDGE,"E67")])]})]});
            fillet(context, id + "F14", {"entities" : qUnion([Q0, Q1, Q2, Q3, Q4, Q5]), "radius" : 3 * mm, "tangentPropagation" : true, "allowEdgeOverflow" : false});
        }
        {
            var Q0;
            Q0=makeQuery(id+"F1.opExtrude","CAP_EDGE",EDGE,{"disambiguationData":[OSD([sQuery(id+"F0.wireOp",EDGE,"E1.bottom")])],"isStart":false});
            fillet(context, id + "F15", {"entities" : qUnion([Q0]), "radius" : 2 * mm, "tangentPropagation" : true, "allowEdgeOverflow" : false});
        }
        {
            var Q0;
            {var subQ0=sQuery(id+"F0.wireOp",EDGE,"E22.filletArc");var subQ1=sQuery(id+"F0.wireOp",EDGE,"E7");var subQ2=sQuery(id+"F0.wireOp",EDGE,"E6");var subQ3=sQuery(id+"F0.wireOp",EDGE,"E5");var subQ4=sQuery(id+"F0.wireOp",EDGE,"E4");var subQ5=sQuery(id+"F0.wireOp",EDGE,"E1.bottom");var subQ6=sQuery(id+"F0.wireOp",EDGE,"E21.filletArc");var subQ7=sQuery(id+"F0.wireOp",EDGE,"E1.top");var subQ8=sQuery(id+"F0.wireOp",EDGE,"E1.left");var subQ9=sQuery(id+"F0.wireOp",EDGE,"E1.right");var subQ10=sQuery(id+"F0.wireOp",EDGE,"E23.filletArc");var subQ11=sQuery(id+"F0.wireOp",EDGE,"E24.filletArc");Q0=makeQuery(id+"F2.boolean.opBoolean","SPLIT",FACE,{"disambiguationData":[TD([makeQuery(id+"F1.opExtrude","SWEPT_FACE",FACE,{"disambiguationData":[OSD([subQ5])]})])],"derivedFrom":makeQuery(id+"F1.opExtrude","CAP_FACE",FACE,{"disambiguationData":[OSD([subQ5,subQ7,subQ8,subQ9,subQ4,subQ3,subQ2,subQ1,subQ6,subQ0,subQ10,subQ11])],"isStart":true})});}
            var sketch = newSketch(context, id + "F16", { "sketchPlane" : qUnion([Q0])});
            skSolve(sketch);
        }
        {
            var Q0;
            Q0=makeQuery(id+"F16.imprint","IMPRINT",FACE,{"disambiguationData":[TD([[makeQuery(id+"F16.imprint","IMPRINT",EDGE,{"derivedFrom":makeQuery(id+"F1.opExtrude","CAP_EDGE",EDGE,{"disambiguationData":[OSD([sQuery(id+"F0.wireOp",EDGE,"E1.bottom")])],"isStart":true})}),1.0]])]});
            var sketch = newSketch(context, id + "F17", { "sketchPlane" : qUnion([Q0])});
            skSolve(sketch);
        }
        {
            var Q0;
            Q0=makeQuery(id+"F16.imprint","IMPRINT",FACE,{"disambiguationData":[TD([[makeQuery(id+"F16.imprint","IMPRINT",EDGE,{"derivedFrom":makeQuery(id+"F1.opExtrude","CAP_EDGE",EDGE,{"disambiguationData":[OSD([sQuery(id+"F0.wireOp",EDGE,"E1.bottom")])],"isStart":true})}),1.0]])]});
            var sketch = newSketch(context, id + "F18", { "sketchPlane" : qUnion([Q0])});
            skLineSegment(sketch, "E79", {"start": v(-149.09, -10.36) * mm, "end": v(-97.11, -55.3) * mm});
            skLineSegment(sketch, "E80", {"start": v(-97.11, -55.3) * mm, "end": v(-97.11, 53.73) * mm});
            skLineSegment(sketch, "E81", {"start": v(-97.11, 53.73) * mm, "end": v(-147.52, 20.52) * mm});
            skLineSegment(sketch, "E82", {"start": v(-147.52, 20.52) * mm, "end": v(-149.09, 18.7) * mm});
            skArc(sketch, "E83", {"start": v(-149.09, 18.7) * mm, "mid": v(-180.6, 4.18) * mm, "end": v(-149.09, -10.36) * mm});
            skLineSegment(sketch, "E84", {"start": v(96.33, 54.52) * mm, "end": v(96.33, -54.52) * mm});
            skLineSegment(sketch, "E85", {"start": v(96.33, -54.52) * mm, "end": v(146.74, -10.36) * mm});
            skLineSegment(sketch, "E86", {"start": v(146.74, -10.36) * mm, "end": v(96.33, -54.52) * mm});
            skLineSegment(sketch, "E87", {"start": v(96.33, 54.52) * mm, "end": v(146.74, 20.52) * mm});
            skArc(sketch, "E88", {"start": v(146.74, -10.36) * mm, "mid": v(177.5, 5.08) * mm, "end": v(146.74, 20.52) * mm});
            skSolve(sketch);
        }
        {
            var Q0;
            Q0=makeQuery(id+"F16.imprint","IMPRINT",FACE,{"disambiguationData":[TD([[makeQuery(id+"F16.imprint","IMPRINT",EDGE,{"derivedFrom":makeQuery(id+"F1.opExtrude","CAP_EDGE",EDGE,{"disambiguationData":[OSD([sQuery(id+"F0.wireOp",EDGE,"E1.bottom")])],"isStart":true})}),1.0]])]});
            var Q1;
            Q1=makeQuery(id+"F18.imprint","IMPRINT",FACE,{"disambiguationData":[TD([[makeQuery(id+"F18.imprint","IMPRINT",EDGE,{"derivedFrom":sQuery(id+"F18.wireOp",EDGE,"E79")}),1.0]])]});
            var Q2;
            Q2=makeQuery(id+"F18.imprint","IMPRINT",FACE,{"disambiguationData":[TD([[makeQuery(id+"F18.imprint","IMPRINT",EDGE,{"derivedFrom":sQuery(id+"F18.wireOp",EDGE,"E84")}),1.0]])]});
            extrude(context, id + "F19", {"entities" : qUnion([Q0, Q1, Q2]), "operationType" : NewBodyOperationType.ADD, "depth" : 25 * mm});
        }
        {
            var Q0;
            Q0=makeQuery(id+"F19.opExtrude","SWEPT_BODY",BODY,{"disambiguationData":[OSD([sQuery(id+"F18.wireOp",EDGE,"E79"),sQuery(id+"F18.wireOp",EDGE,"E80"),sQuery(id+"F18.wireOp",EDGE,"E81"),sQuery(id+"F18.wireOp",EDGE,"E82"),sQuery(id+"F18.wireOp",EDGE,"E83")])]});
            deleteBodies(context, id + "F20", {"entities" : qUnion([Q0])});
        }
        {
            var Q0;
            Q0=makeQuery(id+"F19.opExtrude","SWEPT_BODY",BODY,{"disambiguationData":[OSD([sQuery(id+"F18.wireOp",EDGE,"E84"),sQuery(id+"F18.wireOp",EDGE,"E86"),sQuery(id+"F18.wireOp",EDGE,"E87"),sQuery(id+"F18.wireOp",EDGE,"E88")])]});
            deleteBodies(context, id + "F21", {"entities" : qUnion([Q0])});
        }
    });
